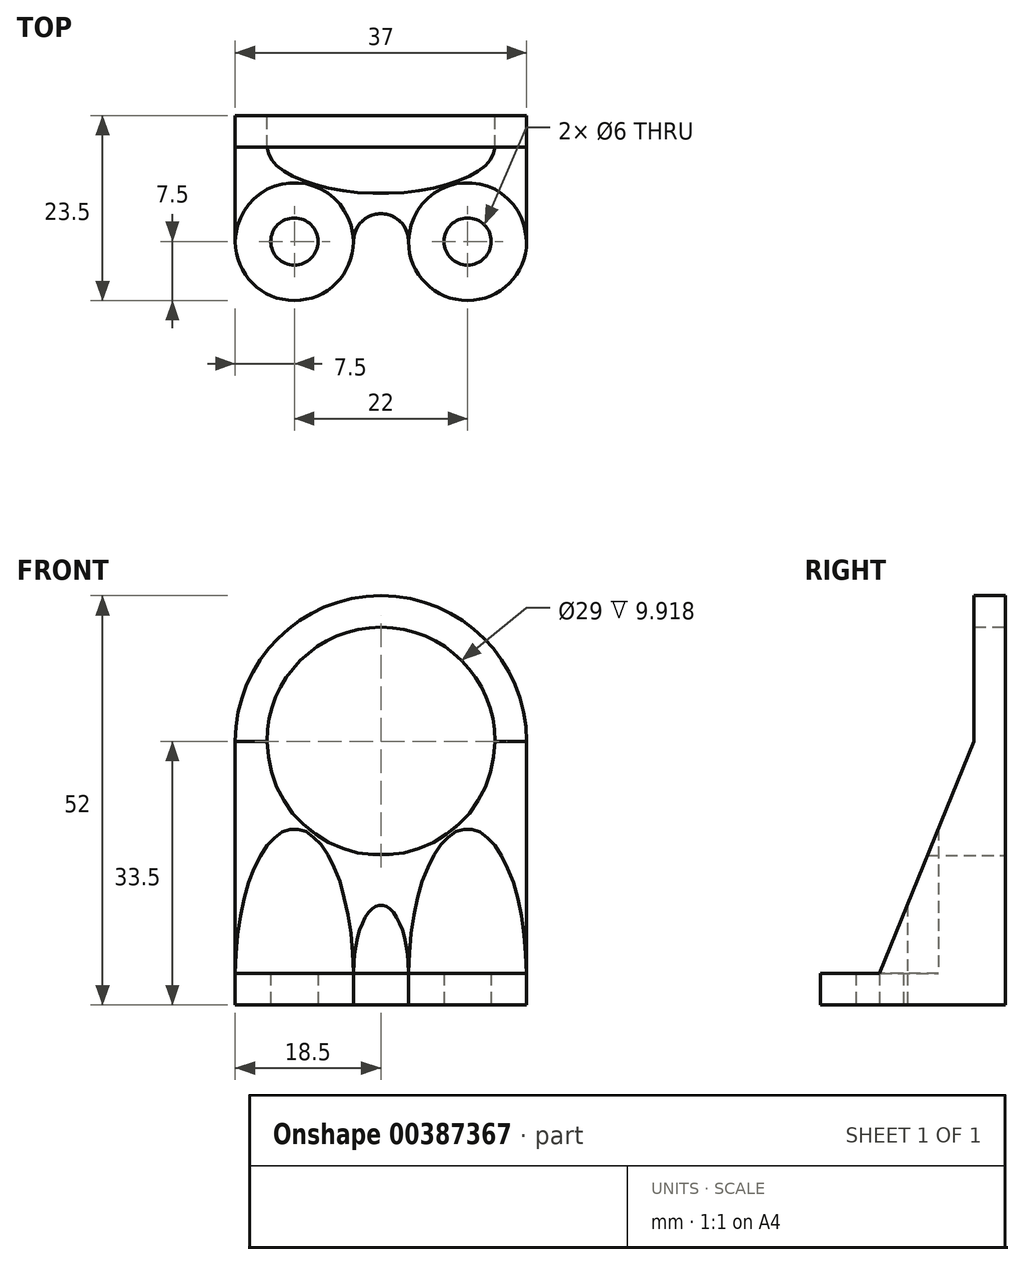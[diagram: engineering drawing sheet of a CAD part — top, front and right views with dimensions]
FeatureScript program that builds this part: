
annotation { "Feature Type Name" : "Feature", "Feature Type Description" : "" }
export const myFeature = defineFeature(function(context is Context, id is Id, definition is map)
    precondition{}
    {
        {
            var Q0;
            Q0=qCreatedBy(makeId("Front.planeOp"),FACE);
            var sketch = newSketch(context, id + "F0", { "sketchPlane" : qUnion([Q0])});
            skPoint(sketch, "E0", {"position": v(25.5, 0) * mm});
            skPoint(sketch, "E1", {"position": v(-25.5, 0) * mm});
            skCircle(sketch, "E2", {"center": v(0, 0) * mm, "radius": 14.5 * mm});
            skArc(sketch, "E3", {"start": v(-18.5, 0) * mm, "mid": v(0, 18.5) * mm, "end": v(18.5, 0) * mm});
            skLineSegment(sketch, "E4", {"start": v(0, 0) * mm, "end": v(0, -33.5) * mm, "construction": true});
            skLineSegment(sketch, "E5", {"start": v(0, -33.5) * mm, "end": v(-18.5, -33.5) * mm});
            skLineSegment(sketch, "E6", {"start": v(0, -33.5) * mm, "end": v(18.5, -33.5) * mm});
            skLineSegment(sketch, "E7", {"start": v(18.5, 0) * mm, "end": v(18.5, -33.5) * mm});
            skLineSegment(sketch, "E8", {"start": v(-18.5, 0) * mm, "end": v(-18.5, -33.5) * mm});
            skSolve(sketch);
        }
        {
            var Q0;
            Q0=makeQuery(id+"F0.imprint","IMPRINT",FACE,{"disambiguationData":[TD([[makeQuery(id+"F0.imprint","IMPRINT",EDGE,{"derivedFrom":sQuery(id+"F0.wireOp",EDGE,"E2")}),-1.0]])]});
            extrude(context, id + "F1", {"entities" : qUnion([Q0]), "depth" : 4 * mm, "offsetDistance" : 25 * mm});
        }
        {
            var Q0;
            Q0=makeQuery(id+"F1.opExtrude","SWEPT_FACE",FACE,{"disambiguationData":[OSD([sQuery(id+"F0.wireOp",EDGE,"E5"),sQuery(id+"F0.wireOp",EDGE,"E6")])]});
            var sketch = newSketch(context, id + "F2", { "sketchPlane" : qUnion([Q0])});
            skLineSegment(sketch, "E9", {"start": v(-18.5, 0) * mm, "end": v(-18.5, 16) * mm});
            skLineSegment(sketch, "E10", {"start": v(18.5, 0) * mm, "end": v(18.5, 16) * mm});
            skLineSegment(sketch, "E11", {"start": v(18.5, 0) * mm, "end": v(-18.5, 0) * mm});
            skLineSegment(sketch, "E12", {"start": v(18.5, 16) * mm, "end": v(11, 16) * mm, "construction": true});
            skLineSegment(sketch, "E13", {"start": v(-18.5, 16) * mm, "end": v(-11, 16) * mm, "construction": true});
            skPoint(sketch, "E14", {"position": v(11, 16) * mm});
            skPoint(sketch, "E15", {"position": v(-11, 16) * mm});
            skCircle(sketch, "E16", {"center": v(11, 16) * mm, "radius": 3 * mm});
            skCircle(sketch, "E17", {"center": v(-11, 16) * mm, "radius": 3 * mm});
            skLineSegment(sketch, "E18", {"start": v(11, 16) * mm, "end": v(-11, 16) * mm, "construction": true});
            skArc(sketch, "E19", {"start": v(18.5, 16) * mm, "mid": v(11, 23.5) * mm, "end": v(3.5, 16) * mm});
            skArc(sketch, "E20", {"start": v(-18.5, 16) * mm, "mid": v(-11, 23.5) * mm, "end": v(-3.5, 16) * mm});
            skArc(sketch, "E21", {"start": v(-3.5, 16) * mm, "mid": v(0, 12.46) * mm, "end": v(3.5, 16) * mm});
            skSolve(sketch);
        }
        {
            var Q0;
            Q0=makeQuery(id+"F2.imprint","IMPRINT",FACE,{"disambiguationData":[TD([[makeQuery(id+"F2.imprint","IMPRINT",EDGE,{"derivedFrom":sQuery(id+"F2.wireOp",EDGE,"E16")}),-1.0]])]});
            extrude(context, id + "F3", {"entities" : qUnion([Q0]), "operationType" : NewBodyOperationType.ADD, "oppositeDirection" : true, "depth" : 4 * mm, "offsetDistance" : 25 * mm});
        }
        {
            var Q0;
            Q0=makeQuery(id+"F3.boolean.opBoolean","MERGE",FACE,{"derivedFrom":[makeQuery(id+"F1.opExtrude","SWEPT_FACE",FACE,{"disambiguationData":[OSD([sQuery(id+"F0.wireOp",EDGE,"E7")])]}),makeQuery(id+"F3.opExtrude","SWEPT_FACE",FACE,{"disambiguationData":[OSD([sQuery(id+"F2.wireOp",EDGE,"E10")])]})]});
            var sketch = newSketch(context, id + "F4", { "sketchPlane" : qUnion([Q0])});
            skLineSegment(sketch, "E22", {"start": v(-16, -29.5) * mm, "end": v(-4, 0) * mm});
            skLineSegment(sketch, "E23", {"start": v(-4, 0) * mm, "end": v(-4, -29.5) * mm});
            skLineSegment(sketch, "E24", {"start": v(-4, -29.5) * mm, "end": v(-16, -29.5) * mm});
            skLineSegment(sketch, "E25", {"start": v(-16, -29.5) * mm, "end": v(-16, 0) * mm});
            skLineSegment(sketch, "E26", {"start": v(-16, 0) * mm, "end": v(-4, 0) * mm});
            skSolve(sketch);
        }
        {
            var Q0;
            Q0=makeQuery(id+"F3.opExtrude","CAP_FACE",FACE,{"disambiguationData":[OSD([sQuery(id+"F0.wireOp",EDGE,"E5"),sQuery(id+"F0.wireOp",EDGE,"E6"),sQuery(id+"F2.wireOp",EDGE,"E9"),sQuery(id+"F2.wireOp",EDGE,"E10"),sQuery(id+"F2.wireOp",EDGE,"E16"),sQuery(id+"F2.wireOp",EDGE,"E17"),sQuery(id+"F2.wireOp",EDGE,"E19"),sQuery(id+"F2.wireOp",EDGE,"E20"),sQuery(id+"F2.wireOp",EDGE,"E21")])],"isStart":false});
            var sketch = newSketch(context, id + "F5", { "sketchPlane" : qUnion([Q0])});
            skLineSegment(sketch, "E27", {"start": v(-18.5, -4) * mm, "end": v(-18.5, -16) * mm});
            skLineSegment(sketch, "E28", {"start": v(-18.5, -16) * mm, "end": v(-14, -16) * mm});
            skLineSegment(sketch, "E29", {"start": v(-8, -16) * mm, "end": v(-3.5, -16) * mm});
            skLineSegment(sketch, "E30", {"start": v(3.5, -16) * mm, "end": v(8, -16) * mm});
            skLineSegment(sketch, "E31", {"start": v(14, -16) * mm, "end": v(18.5, -16) * mm});
            skLineSegment(sketch, "E32", {"start": v(18.5, -16) * mm, "end": v(18.5, -4) * mm});
            skLineSegment(sketch, "E33", {"start": v(18.5, -4) * mm, "end": v(-18.5, -4) * mm});
            skArc(sketch, "E34", {"start": v(-3.5, -16) * mm, "mid": v(-11, -8.5) * mm, "end": v(-18.5, -16) * mm});
            skArc(sketch, "E35", {"start": v(3.5, -16) * mm, "mid": v(0, -12.45) * mm, "end": v(-3.5, -16) * mm});
            skArc(sketch, "E36", {"start": v(18.5, -16) * mm, "mid": v(11, -8.5) * mm, "end": v(3.5, -16) * mm});
            skSolve(sketch);
        }
        {
            var Q0;
            {var subQ1=sQuery(id+"F5.wireOp",EDGE,"E27");Q0=makeQuery(id+"F5.imprint","IMPRINT",FACE,{"disambiguationData":[TD([[makeQuery(id+"F5.imprint","IMPRINT",EDGE,{"derivedFrom":subQ1}),1.0]])]});}
            extrude(context, id + "F6", {"entities" : qUnion([Q0]), "operationType" : NewBodyOperationType.ADD, "depth" : 29.5 * mm, "offsetDistance" : 25 * mm});
        }
        {
            var Q0;
            Q0=sQuery(id+"F0.wireOp",VERTEX,"E4.start");
            var Q1;
            Q1=makeQuery(id+"F1.opExtrude","SWEPT_BODY",BODY,{"disambiguationData":[OSD([sQuery(id+"F0.wireOp",EDGE,"E2"),sQuery(id+"F0.wireOp",EDGE,"E3"),sQuery(id+"F0.wireOp",EDGE,"E5"),sQuery(id+"F0.wireOp",EDGE,"E6"),sQuery(id+"F0.wireOp",EDGE,"E7"),sQuery(id+"F0.wireOp",EDGE,"E8")])]});
            hole(context, id + "F7", {"style" : HoleStyle.SIMPLE, "endStyle" : HoleEndStyle.THROUGH, "oppositeDirection" : true, "holeDiameter" : 29 * mm, "majorDiameter" : 5 * mm, "isTappedThrough" : true, "tappedDepth" : 12 * mm, "tapClearance" : 3, "locations" : qUnion([Q0]), "scope" : qUnion([Q1])});
        }
        {
            var Q0;
            Q0=makeQuery(id+"F4.imprint","IMPRINT",FACE,{"disambiguationData":[TD([[makeQuery(id+"F4.imprint","IMPRINT",EDGE,{"derivedFrom":sQuery(id+"F4.wireOp",EDGE,"E22")}),1.0]])]});
            extrude(context, id + "F8", {"entities" : qUnion([Q0]), "operationType" : NewBodyOperationType.REMOVE, "oppositeDirection" : true, "depth" : 37 * mm, "offsetDistance" : 25 * mm});
        }
    });
